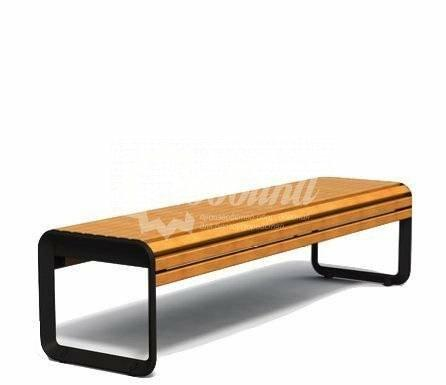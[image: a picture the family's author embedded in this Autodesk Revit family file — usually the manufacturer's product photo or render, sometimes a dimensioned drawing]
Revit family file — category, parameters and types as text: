
# Revit family: Банкетка чугунная «Варшава» Арт 12299
name_source: partatom
category: Антураж
revit_build: Autodesk Revit 2018 (Build: 20180423_1000(x64)
units: mm (PartAtom-declared; Revit-internal decimal feet)

## family parameters
Всегда вертикально = Да
Источник визуального образа = Геометрия семейства
На основе рабочей плоскости = Нет
Общий = Нет
При загрузке вырезать с полостями = Нет
Точка расчета площади = Нет

## types (6) — shared parameters
URL = https://hobbyka.ru
Артикул товара = Арт. 12299
Высота = 450 мм
Группа модели = Скамейки
Изготовитель = ООО «Хоббика»
Изображение типоразмера = Банкетка чугунная «Варшава» Арт 12299.jpg
Материал изделия = Сталь, чугун, дерево
Цвет лавки = Дерево
Цвет опоры = Чугун
Ширина = 500 мм

## per-type parameters (varying)
| type | Версия 0,6 м (кресло) | Версия 1,2 м | Версия 1,5 м | Версия 1,8 м | Версия 2,0 м (3 опоры) | Версия 3,0 м (3 опоры) | Длина | Описание | Средняя опора |
| Версия 0,6 м (кресло) | Да | Нет | Нет | Нет | Нет | Нет | 600 мм | Банкетка чугунная «Варшава». Версия 0,6 м (кресло) | Нет |
| Версия 1,2 м | Нет | Да | Нет | Нет | Нет | Нет | 1200 мм | Банкетка чугунная «Варшава». Версия 1,2 м | Нет |
| Версия 1,5 м | Нет | Нет | Да | Нет | Нет | Нет | 1500 мм | Банкетка чугунная «Варшава». Версия 1,5 м | Нет |
| Версия 1,8 м | Нет | Нет | Нет | Да | Нет | Нет | 1800 мм | Банкетка чугунная «Варшава». Версия 1,8 м | Нет |
| Версия 2,0 м (3 опоры) | Нет | Нет | Нет | Нет | Да | Нет | 2000 мм | Банкетка чугунная «Варшава». Версия 2,0 м (3 опоры) | Да |
| Версия 3,0  м (3 опоры) | Нет | Нет | Нет | Нет | Нет | Да | 3000 мм | Банкетка чугунная «Варшава». Версия 3,0 м (3 опоры) | Да |
